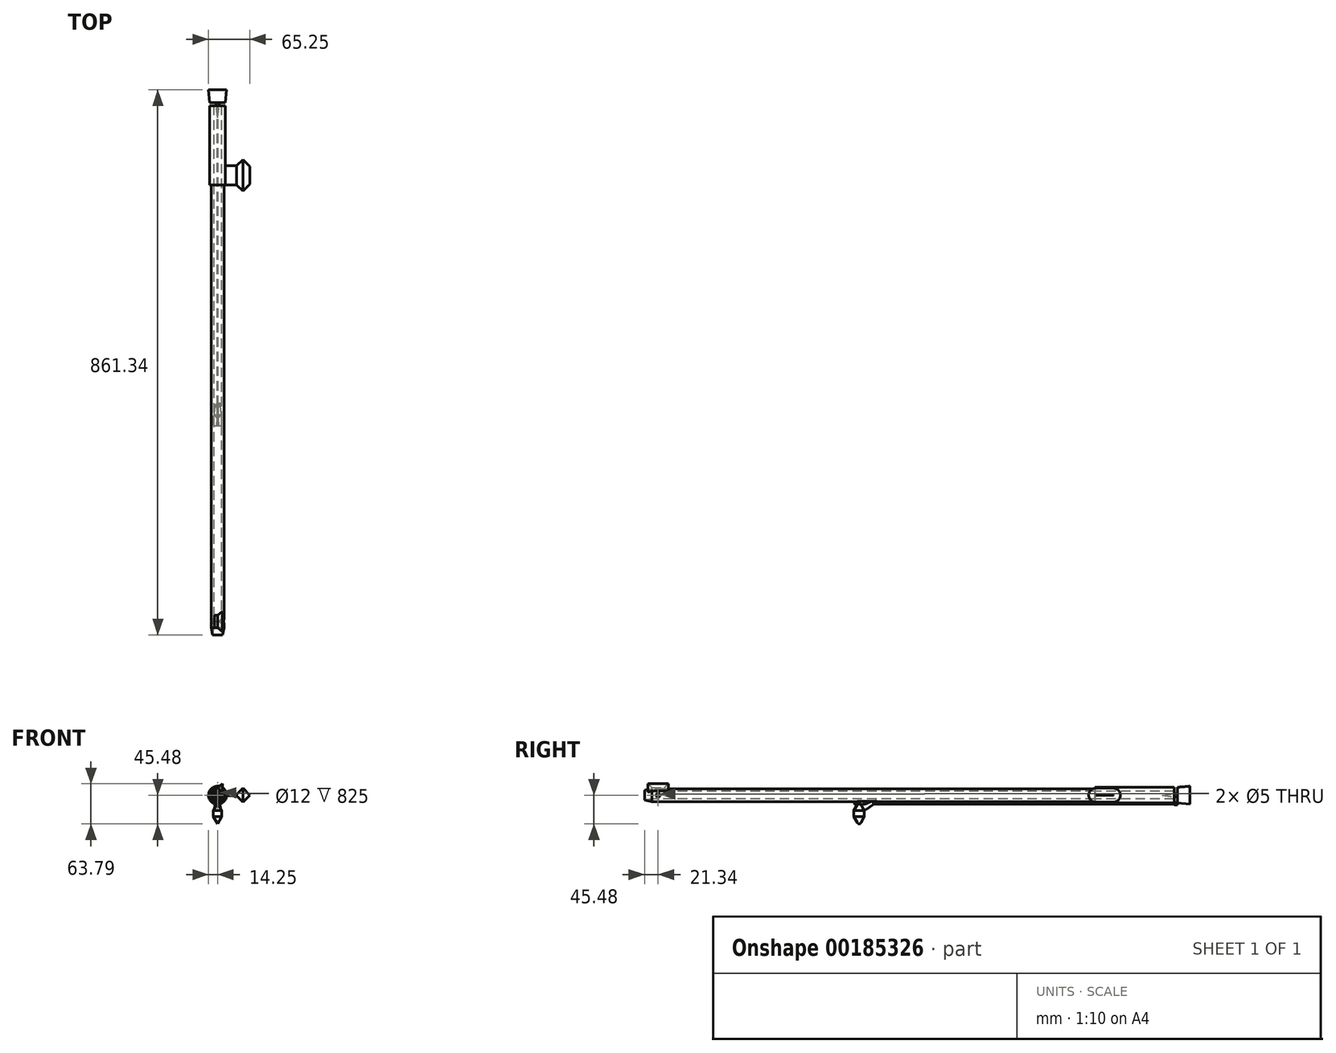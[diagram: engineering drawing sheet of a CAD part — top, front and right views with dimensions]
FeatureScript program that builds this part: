
annotation { "Feature Type Name" : "Feature", "Feature Type Description" : "" }
export const myFeature = defineFeature(function(context is Context, id is Id, definition is map)
    precondition{}
    {
        {
            var Q0;
            Q0=qCreatedBy(makeId("Front.planeOp"),FACE);
            var sketch = newSketch(context, id + "F0", { "sketchPlane" : qUnion([Q0])});
            skCircle(sketch, "E0", {"center": v(0, 0) * mm, "radius": 6 * mm});
            skCircle(sketch, "E1", {"center": v(0, 0) * mm, "radius": 10 * mm});
            skSolve(sketch);
        }
        {
            var Q0;
            Q0=makeQuery(id+"F0.imprint","IMPRINT",FACE,{"disambiguationData":[TD([[makeQuery(id+"F0.imprint","IMPRINT",EDGE,{"derivedFrom":sQuery(id+"F0.wireOp",EDGE,"E0")}),-1.0]])]});
            extrude(context, id + "F1", {"entities" : qUnion([Q0]), "oppositeDirection" : true, "depth" : 700 * mm});
        }
        {
            var Q0;
            Q0=makeQuery(id+"F1.opExtrude","CAP_FACE",FACE,{"disambiguationData":[OSD([sQuery(id+"F0.wireOp",EDGE,"E0"),sQuery(id+"F0.wireOp",EDGE,"E1")])],"isStart":false});
            var sketch = newSketch(context, id + "F2", { "sketchPlane" : qUnion([Q0])});
            skArc(sketch, "E2", {"start": v(0, -10) * mm, "mid": v(10.04, 0) * mm, "end": v(0, 10) * mm});
            skArc(sketch, "E3", {"start": v(0, -6) * mm, "mid": v(5.98, 0) * mm, "end": v(0, 6) * mm});
            skLineSegment(sketch, "E4", {"start": v(0, 6) * mm, "end": v(0, 10) * mm});
            skLineSegment(sketch, "E5", {"start": v(0, -6) * mm, "end": v(0, -10) * mm});
            skSolve(sketch);
        }
        {
            var Q0;
            Q0 = qSketchRegion(id + "F2", true);
            extrude(context, id + "F3", {"entities" : qUnion([Q0]), "operationType" : NewBodyOperationType.ADD, "depth" : 100 * mm});
        }
        {
            var Q0;
            Q0=makeQuery(id+"F1.opExtrude","CAP_FACE",FACE,{"disambiguationData":[OSD([sQuery(id+"F0.wireOp",EDGE,"E0"),sQuery(id+"F0.wireOp",EDGE,"E1")])],"isStart":false});
            var sketch = newSketch(context, id + "F4", { "sketchPlane" : qUnion([Q0])});
            skArc(sketch, "E6", {"start": v(0, 10) * mm, "mid": v(-10, 0) * mm, "end": v(0, -10) * mm});
            skLineSegment(sketch, "E7", {"start": v(0, 10) * mm, "end": v(0, 6) * mm});
            skLineSegment(sketch, "E8", {"start": v(0, -10) * mm, "end": v(0, -6) * mm});
            skArc(sketch, "E9", {"start": v(0, 6) * mm, "mid": v(-6, 0) * mm, "end": v(0, -6) * mm});
            skCircle(sketch, "E10", {"center": v(0, 0) * mm, "radius": 12.5 * mm});
            skCircle(sketch, "E11", {"center": v(0, 0) * mm, "radius": 10 * mm});
            skSolve(sketch);
        }
        {
            var Q0;
            Q0 = qSketchRegion(id + "F4", true);
            extrude(context, id + "F5", {"entities" : qUnion([Q0]), "depth" : 100 * mm});
        }
        {
            var Q0;
            Q0=makeQuery(id+"F1.opExtrude","CAP_FACE",FACE,{"disambiguationData":[OSD([sQuery(id+"F0.wireOp",EDGE,"E0"),sQuery(id+"F0.wireOp",EDGE,"E1")])],"isStart":false});
            extrude(context, id + "F6", {"entities" : qUnion([Q0]), "operationType" : NewBodyOperationType.ADD, "depth" : 100 * mm});
        }
        {
            var Q0;
            Q0=makeQuery(id+"F3.opExtrude","CAP_FACE",FACE,{"disambiguationData":[OSD([sQuery(id+"F2.wireOp",EDGE,"E2"),sQuery(id+"F2.wireOp",EDGE,"E3"),sQuery(id+"F2.wireOp",EDGE,"E4"),sQuery(id+"F2.wireOp",EDGE,"E5")])],"isStart":false});
            var sketch = newSketch(context, id + "F7", { "sketchPlane" : qUnion([Q0])});
            skCircle(sketch, "E12", {"center": v(0, 0) * mm, "radius": 12.5 * mm});
            skSolve(sketch);
        }
        {
            var Q0;
            Q0=makeQuery(id+"F7.imprint","IMPRINT",FACE,{"disambiguationData":[TD([[makeQuery(id+"F7.imprint","IMPRINT",EDGE,{"derivedFrom":sQuery(id+"F7.wireOp",EDGE,"E12")}),1.0]])]});
            var Q1;
            Q1=makeQuery(id+"F7.imprint","IMPRINT",FACE,{"disambiguationData":[TD([[makeQuery(id+"F7.imprint","IMPRINT",EDGE,{"derivedFrom":makeQuery(id+"F3.opExtrude","CAP_EDGE",EDGE,{"disambiguationData":[OSD([sQuery(id+"F2.wireOp",EDGE,"E2")])],"isStart":false})}),1.0]])]});
            extrude(context, id + "F8", {"entities" : qUnion([Q0, Q1]), "operationType" : NewBodyOperationType.ADD, "depth" : 25 * mm});
        }
        {
            var Q0;
            Q0=makeQuery(id+"F6.boolean.opBoolean","MERGE",FACE,{"derivedFrom":[makeQuery(id+"F5.opExtrude","CAP_FACE",FACE,{"disambiguationData":[OSD([sQuery(id+"F4.wireOp",EDGE,"E10"),sQuery(id+"F4.wireOp",EDGE,"E11")])],"isStart":true}),makeQuery(id+"F6.opExtrude","CAP_FACE",FACE,{"disambiguationData":[OSD([sQuery(id+"F0.wireOp",EDGE,"E0"),sQuery(id+"F0.wireOp",EDGE,"E1")])],"isStart":true})]});
            var sketch = newSketch(context, id + "F9", { "sketchPlane" : qUnion([Q0])});
            skLineSegment(sketch, "E13", {"start": v(10, 0) * mm, "end": v(10, 1) * mm});
            skLineSegment(sketch, "E14", {"start": v(10, 1) * mm, "end": v(30, 1) * mm});
            skLineSegment(sketch, "E15", {"start": v(30, 1) * mm, "end": v(30, -1) * mm});
            skLineSegment(sketch, "E16", {"start": v(30, -1) * mm, "end": v(10, -1) * mm});
            skLineSegment(sketch, "E17", {"start": v(10, -1) * mm, "end": v(10, 0) * mm});
            skSolve(sketch);
        }
        {
            var Q0;
            {var subQ0=sQuery(id+"F9.wireOp",EDGE,"E15");Q0=makeQuery(id+"F9.imprint","IMPRINT",FACE,{"disambiguationData":[TD([[makeQuery(id+"F9.imprint","IMPRINT",EDGE,{"derivedFrom":subQ0}),-1.0]])]});}
            extrude(context, id + "F10", {"entities" : qUnion([Q0]), "operationType" : NewBodyOperationType.ADD, "oppositeDirection" : true, "depth" : 30 * mm});
        }
        {
            var Q0;
            Q0=makeQuery(id+"F10.opExtrude","CAP_EDGE",EDGE,{"disambiguationData":[OSD([sQuery(id+"F9.wireOp",EDGE,"E16")])],"isStart":true});
            var Q1;
            Q1=makeQuery(id+"F10.opExtrude","CAP_EDGE",EDGE,{"disambiguationData":[OSD([sQuery(id+"F9.wireOp",EDGE,"E14")])],"isStart":true});
            var Q2;
            Q2=makeQuery(id+"F10.opExtrude","CAP_EDGE",EDGE,{"disambiguationData":[OSD([sQuery(id+"F9.wireOp",EDGE,"E14")])],"isStart":false});
            var Q3;
            Q3=makeQuery(id+"F10.opExtrude","CAP_EDGE",EDGE,{"disambiguationData":[OSD([sQuery(id+"F9.wireOp",EDGE,"E16")])],"isStart":false});
            fillet(context, id + "F11", {"entities" : qUnion([Q0, Q1, Q2, Q3]), "radius" : 1 * mm, "tangentPropagation" : true, "allowEdgeOverflow" : false});
        }
        {
            var Q0;
            Q0=makeQuery(id+"F10.opExtrude","SWEPT_FACE",FACE,{"disambiguationData":[OSD([sQuery(id+"F9.wireOp",EDGE,"E15")])]});
            extrude(context, id + "F12", {"entities" : qUnion([Q0]), "operationType" : NewBodyOperationType.ADD, "depth" : 10 * mm, "hasDraft" : true, "draftAngle" : 45 * degree});
        }
        {
            var Q0;
            Q0=makeQuery(id+"F12.opExtrude","CAP_FACE",FACE,{"disambiguationData":[OSD([sQuery(id+"F9.wireOp",EDGE,"E15")])],"isStart":false});
            extrude(context, id + "F13", {"entities" : qUnion([Q0]), "operationType" : NewBodyOperationType.ADD, "depth" : 25 * mm, "hasDraft" : true, "draftAngle" : 45 * degree, "draftPullDirection" : true});
        }
        {
            var Q0;
            Q0=makeQuery(id+"F8.opExtrude","CAP_FACE",FACE,{"disambiguationData":[OSD([sQuery(id+"F7.wireOp",EDGE,"E12")])],"isStart":false});
            var sketch = newSketch(context, id + "F14", { "sketchPlane" : qUnion([Q0])});
            skPoint(sketch, "E18", {"position": v(0, 0) * mm});
            skSolve(sketch);
        }
        {
            var Q0;
            Q0=sQuery(id+"F14.wireOp",VERTEX,"E18");
            var Q1;
            Q1=makeQuery(id+"F1.opExtrude","SWEPT_BODY",BODY,{"disambiguationData":[OSD([sQuery(id+"F0.wireOp",EDGE,"E0"),sQuery(id+"F0.wireOp",EDGE,"E1")])]});
            hole(context, id + "F15", {"style" : HoleStyle.SIMPLE, "endStyle" : HoleEndStyle.THROUGH, "holeDiameter" : 5 * mm, "locations" : qUnion([Q0]), "scope" : qUnion([Q1]), "isTappedThrough" : true});
        }
        {
            var Q0;
            Q0=makeQuery(id+"F8.opExtrude","CAP_FACE",FACE,{"disambiguationData":[OSD([sQuery(id+"F7.wireOp",EDGE,"E12")])],"isStart":false});
            var sketch = newSketch(context, id + "F16", { "sketchPlane" : qUnion([Q0])});
            skCircle(sketch, "E19", {"center": v(0, 0) * mm, "radius": 2.5 * mm});
            skSolve(sketch);
        }
        {
            var Q0;
            Q0 = qSketchRegion(id + "F16", true);
            extrude(context, id + "F17", {"entities" : qUnion([Q0]), "oppositeDirection" : true, "depth" : 20 * mm, "hasDraft" : true, "draftAngle" : 7.5 * degree, "draftPullDirection" : true});
        }
        {
            var Q0;
            Q0=makeQuery(id+"F17.opExtrude","CAP_FACE",FACE,{"disambiguationData":[OSD([sQuery(id+"F16.wireOp",EDGE,"E19")])],"isStart":true});
            extrude(context, id + "F18", {"entities" : qUnion([Q0]), "operationType" : NewBodyOperationType.ADD, "depth" : 5 * mm});
        }
        {
            var Q0;
            Q0=makeQuery(id+"F18.opExtrude","CAP_FACE",FACE,{"disambiguationData":[OSD([sQuery(id+"F16.wireOp",EDGE,"E19")])],"isStart":false});
            var sketch = newSketch(context, id + "F19", { "sketchPlane" : qUnion([Q0])});
            skCircle(sketch, "E20", {"center": v(0, 0) * mm, "radius": 12.5 * mm});
            skSolve(sketch);
        }
        {
            var Q0;
            Q0 = qSketchRegion(id + "F19", true);
            extrude(context, id + "F20", {"entities" : qUnion([Q0]), "operationType" : NewBodyOperationType.ADD, "depth" : 20 * mm, "hasDraft" : true, "draftAngle" : 5 * degree});
        }
        {
            var Q0;
            Q0=makeQuery(id+"F8.opExtrude","CAP_FACE",FACE,{"disambiguationData":[OSD([sQuery(id+"F7.wireOp",EDGE,"E12")])],"isStart":false});
            var sketch = newSketch(context, id + "F21", { "sketchPlane" : qUnion([Q0])});
            skLineSegment(sketch, "E21", {"start": v(0, -12.5) * mm, "end": v(0, -13.5) * mm});
            skLineSegment(sketch, "E22.bottom", {"start": v(0.5, -15.25) * mm, "end": v(-0.5, -15.25) * mm});
            skLineSegment(sketch, "E22.top", {"start": v(0.5, -11.75) * mm, "end": v(-0.5, -11.75) * mm});
            skLineSegment(sketch, "E22.left", {"start": v(0.5, -15.25) * mm, "end": v(0.5, -11.75) * mm});
            skLineSegment(sketch, "E22.right", {"start": v(-0.5, -15.25) * mm, "end": v(-0.5, -11.75) * mm});
            skPoint(sketch, "E22.middle", {"position": v(0, -13.5) * mm});
            skSolve(sketch);
        }
        {
            var Q0;
            Q0 = qSketchRegion(id + "F21", true);
            extrude(context, id + "F22", {"entities" : qUnion([Q0]), "depth" : 5 * mm});
        }
        {
            var Q0;
            Q0=makeQuery(id+"F22.opExtrude","CAP_FACE",FACE,{"disambiguationData":[OSD([sQuery(id+"F21.wireOp",EDGE,"E22.bottom"),sQuery(id+"F21.wireOp",EDGE,"E22.top"),sQuery(id+"F21.wireOp",EDGE,"E22.left"),sQuery(id+"F21.wireOp",EDGE,"E22.right")])],"isStart":true});
            var sketch = newSketch(context, id + "F23", { "sketchPlane" : qUnion([Q0])});
            skLineSegment(sketch, "E23", {"start": v(0, -11.75) * mm, "end": v(0, -13.5) * mm});
            skPoint(sketch, "E23.endSnap0", {"position": v(0, -15.25) * mm});
            skCircle(sketch, "E24", {"center": v(0, -13.5) * mm, "radius": 0.5 * mm});
            skSolve(sketch);
        }
        {
            var Q0;
            Q0=makeQuery(id+"F23.imprint","IMPRINT",FACE,{"disambiguationData":[TD([[makeQuery(id+"F23.imprint","IMPRINT",EDGE,{"derivedFrom":sQuery(id+"F23.wireOp",EDGE,"E24")}),1.0]])]});
            extrude(context, id + "F24", {"entities" : qUnion([Q0]), "operationType" : NewBodyOperationType.ADD, "depth" : 500 * mm});
        }
        {
            var Q0;
            Q0=makeQuery(id+"F24.opExtrude","CAP_FACE",FACE,{"disambiguationData":[OSD([sQuery(id+"F23.wireOp",EDGE,"E24")])],"isStart":false});
            var sketch = newSketch(context, id + "F25", { "sketchPlane" : qUnion([Q0])});
            skArc(sketch, "E25", {"start": v(-1, -13.5) * mm, "mid": v(0, -14.5) * mm, "end": v(1, -13.5) * mm});
            skLineSegment(sketch, "E26", {"start": v(-1, -13.5) * mm, "end": v(-1, -9.96) * mm});
            skLineSegment(sketch, "E27", {"start": v(1, -13.5) * mm, "end": v(1, -9.96) * mm});
            skLineSegment(sketch, "E28", {"start": v(-1, -9.96) * mm, "end": v(1, -9.96) * mm});
            skSolve(sketch);
        }
        {
            var Q0;
            Q0=makeQuery(id+"F25.imprint","IMPRINT",FACE,{"disambiguationData":[TD([[makeQuery(id+"F25.imprint","IMPRINT",EDGE,{"derivedFrom":sQuery(id+"F25.wireOp",EDGE,"E25")}),1.0]])]});
            extrude(context, id + "F26", {"entities" : qUnion([Q0]), "operationType" : NewBodyOperationType.ADD, "oppositeDirection" : true, "depth" : 25 * mm});
        }
        {
            var Q0;
            Q0=makeQuery(id+"F24.opExtrude","CAP_FACE",FACE,{"disambiguationData":[OSD([sQuery(id+"F23.wireOp",EDGE,"E24")])],"isStart":false});
            var sketch = newSketch(context, id + "F27", { "sketchPlane" : qUnion([Q0])});
            skCircle(sketch, "E29", {"center": v(0, -13.5) * mm, "radius": 0.5 * mm});
            skLineSegment(sketch, "E30", {"start": v(0, -13) * mm, "end": v(2, -13) * mm});
            skLineSegment(sketch, "E31", {"start": v(0, -14) * mm, "end": v(2, -14) * mm});
            skLineSegment(sketch, "E32", {"start": v(2, -14) * mm, "end": v(2, -13) * mm});
            skSolve(sketch);
        }
        {
            var Q0;
            {var subQ0=sQuery(id+"F27.wireOp",EDGE,"E30");Q0=makeQuery(id+"F27.imprint","IMPRINT",FACE,{"disambiguationData":[TD([[makeQuery(id+"F27.imprint","IMPRINT",EDGE,{"derivedFrom":subQ0}),-1.0]])]});}
            var Q1;
            Q1=makeQuery(id+"F27.imprint","IMPRINT",FACE,{"disambiguationData":[TD([[makeQuery(id+"F27.imprint","IMPRINT",EDGE,{"derivedFrom":sQuery(id+"F27.wireOp",EDGE,"E29")}),1.0]])]});
            extrude(context, id + "F28", {"entities" : qUnion([Q0, Q1]), "operationType" : NewBodyOperationType.ADD, "depth" : 5 * mm});
        }
        {
            var Q0;
            Q0=makeQuery(id+"F26.opExtrude","CAP_FACE",FACE,{"disambiguationData":[OSD([sQuery(id+"F23.wireOp",EDGE,"E24"),sQuery(id+"F25.wireOp",EDGE,"E25"),sQuery(id+"F25.wireOp",EDGE,"E26"),sQuery(id+"F25.wireOp",EDGE,"E27"),sQuery(id+"F25.wireOp",EDGE,"E28")])],"isStart":true});
            var sketch = newSketch(context, id + "F29", { "sketchPlane" : qUnion([Q0])});
            skLineSegment(sketch, "E33", {"start": v(0, -14) * mm, "end": v(0.87, -14) * mm});
            skLineSegment(sketch, "E34", {"start": v(0.87, -14) * mm, "end": v(-0.87, -14) * mm});
            skSolve(sketch);
        }
        {
            var Q0;
            {var subQ0=sQuery(id+"F29.wireOp",EDGE,"E34");var subQ1=makeQuery(id+"F26.opExtrude","CAP_EDGE",EDGE,{"disambiguationData":[OSD([sQuery(id+"F25.wireOp",EDGE,"E25")])],"isStart":true});var subQ2=makeQuery(id+"F29.imprint","INTERSECT",VERTEX,{"disambiguationData":[OD(0.0)],"derivedFrom":[subQ1,subQ0]});Q0=makeQuery(id+"F29.imprint","IMPRINT",FACE,{"disambiguationData":[TD([[makeQuery(id+"F29.imprint","IMPRINT",EDGE,{"disambiguationData":[TD([[subQ2,-1.0]])],"derivedFrom":subQ0}),1.0]])]});}
            extrude(context, id + "F30", {"entities" : qUnion([Q0]), "operationType" : NewBodyOperationType.ADD, "depth" : 5 * mm});
        }
        {
            var Q0;
            Q0=makeQuery(id+"F28.opExtrude","SWEPT_FACE",FACE,{"disambiguationData":[OSD([sQuery(id+"F27.wireOp",EDGE,"E31")])]});
            var sketch = newSketch(context, id + "F31", { "sketchPlane" : qUnion([Q0])});
            skLineSegment(sketch, "E35", {"start": v(0, -320) * mm, "end": v(0, -325) * mm});
            skLineSegment(sketch, "E36", {"start": v(0, -325) * mm, "end": v(-0.85, -325) * mm});
            skLineSegment(sketch, "E37", {"start": v(0, -325) * mm, "end": v(0.85, -325) * mm});
            skLineSegment(sketch, "E38.bottom", {"start": v(-0.85, -325) * mm, "end": v(0.86, -325) * mm});
            skLineSegment(sketch, "E38.top", {"start": v(-0.85, -330.01) * mm, "end": v(0.86, -330.01) * mm});
            skLineSegment(sketch, "E38.left", {"start": v(-0.85, -325) * mm, "end": v(-0.85, -330.01) * mm});
            skLineSegment(sketch, "E38.right", {"start": v(0.86, -325) * mm, "end": v(0.86, -330.01) * mm});
            skSolve(sketch);
        }
        {
            var Q0;
            Q0 = qSketchRegion(id + "F31", true);
            extrude(context, id + "F32", {"entities" : qUnion([Q0]), "operationType" : NewBodyOperationType.ADD, "depth" : 10 * mm, "hasDraft" : true, "draftAngle" : 30 * degree});
        }
        {
            var Q0;
            Q0=makeQuery(id+"F32.opExtrude","CAP_FACE",FACE,{"disambiguationData":[OSD([sQuery(id+"F31.wireOp",EDGE,"E38.bottom"),sQuery(id+"F31.wireOp",EDGE,"E38.top"),sQuery(id+"F31.wireOp",EDGE,"E38.left"),sQuery(id+"F31.wireOp",EDGE,"E38.right")])],"isStart":false});
            extrude(context, id + "F33", {"entities" : qUnion([Q0]), "operationType" : NewBodyOperationType.ADD, "depth" : 10 * mm});
        }
        {
            var Q0;
            Q0=makeQuery(id+"F33.opExtrude","CAP_FACE",FACE,{"disambiguationData":[OSD([sQuery(id+"F31.wireOp",EDGE,"E38.bottom"),sQuery(id+"F31.wireOp",EDGE,"E38.top"),sQuery(id+"F31.wireOp",EDGE,"E38.left"),sQuery(id+"F31.wireOp",EDGE,"E38.right")])],"isStart":false});
            extrude(context, id + "F34", {"entities" : qUnion([Q0]), "operationType" : NewBodyOperationType.ADD, "depth" : 25 * mm, "hasDraft" : true, "draftAngle" : 30 * degree, "draftPullDirection" : true});
        }
        {
            var Q0;
            Q0=makeQuery(id+"F32.opExtrude","SWEPT_EDGE",EDGE,{"disambiguationData":[OSD([sQuery(id+"F31.wireOp",EDGE,"E38.top"),sQuery(id+"F31.wireOp",EDGE,"E38.right")])]});
            var Q1;
            Q1=makeQuery(id+"F32.opExtrude","SWEPT_EDGE",EDGE,{"disambiguationData":[OSD([sQuery(id+"F31.wireOp",EDGE,"E38.top"),sQuery(id+"F31.wireOp",EDGE,"E38.left")])]});
            var Q2;
            Q2=makeQuery(id+"F32.opExtrude","SWEPT_EDGE",EDGE,{"disambiguationData":[OSD([sQuery(id+"F31.wireOp",EDGE,"E38.bottom"),sQuery(id+"F31.wireOp",EDGE,"E38.right")])]});
            var Q3;
            Q3=makeQuery(id+"F32.opExtrude","SWEPT_EDGE",EDGE,{"disambiguationData":[OSD([sQuery(id+"F31.wireOp",EDGE,"E36"),sQuery(id+"F31.wireOp",EDGE,"E38.bottom"),sQuery(id+"F31.wireOp",EDGE,"E38.left")])]});
            var Q4;
            Q4=makeQuery(id+"F33.opExtrude","SWEPT_EDGE",EDGE,{"disambiguationData":[OSD([sQuery(id+"F31.wireOp",EDGE,"E38.bottom"),sQuery(id+"F31.wireOp",EDGE,"E38.right")])]});
            var Q5;
            Q5=makeQuery(id+"F33.opExtrude","SWEPT_EDGE",EDGE,{"disambiguationData":[OSD([sQuery(id+"F31.wireOp",EDGE,"E38.top"),sQuery(id+"F31.wireOp",EDGE,"E38.right")])]});
            var Q6;
            Q6=makeQuery(id+"F33.opExtrude","SWEPT_EDGE",EDGE,{"disambiguationData":[OSD([sQuery(id+"F31.wireOp",EDGE,"E38.top"),sQuery(id+"F31.wireOp",EDGE,"E38.left")])]});
            var Q7;
            Q7=makeQuery(id+"F33.opExtrude","SWEPT_EDGE",EDGE,{"disambiguationData":[OSD([sQuery(id+"F31.wireOp",EDGE,"E36"),sQuery(id+"F31.wireOp",EDGE,"E38.bottom"),sQuery(id+"F31.wireOp",EDGE,"E38.left")])]});
            var Q8;
            Q8=makeQuery(id+"F34.opExtrude","SWEPT_EDGE",EDGE,{"disambiguationData":[OSD([sQuery(id+"F31.wireOp",EDGE,"E36"),sQuery(id+"F31.wireOp",EDGE,"E38.bottom"),sQuery(id+"F31.wireOp",EDGE,"E38.left")])]});
            var Q9;
            Q9=makeQuery(id+"F34.opExtrude","SWEPT_EDGE",EDGE,{"disambiguationData":[OSD([sQuery(id+"F31.wireOp",EDGE,"E38.top"),sQuery(id+"F31.wireOp",EDGE,"E38.left")])]});
            var Q10;
            Q10=makeQuery(id+"F34.opExtrude","SWEPT_EDGE",EDGE,{"disambiguationData":[OSD([sQuery(id+"F31.wireOp",EDGE,"E38.top"),sQuery(id+"F31.wireOp",EDGE,"E38.right")])]});
            var Q11;
            Q11=makeQuery(id+"F34.opExtrude","SWEPT_EDGE",EDGE,{"disambiguationData":[OSD([sQuery(id+"F31.wireOp",EDGE,"E38.bottom"),sQuery(id+"F31.wireOp",EDGE,"E38.right")])]});
            fillet(context, id + "F35", {"entities" : qUnion([Q0, Q1, Q2, Q3, Q4, Q5, Q6, Q7, Q8, Q9, Q10, Q11]), "radius" : 1.5 * mm, "tangentPropagation" : true, "allowEdgeOverflow" : false});
        }
        {
            var Q0;
            Q0=makeQuery(id+"F32.opExtrude","SWEPT_FACE",FACE,{"disambiguationData":[OSD([sQuery(id+"F31.wireOp",EDGE,"E38.top")])]});
            extrude(context, id + "F36", {"entities" : qUnion([Q0]), "operationType" : NewBodyOperationType.ADD, "depth" : 20 * mm, "hasDraft" : true, "draftAngle" : 3 * degree, "draftPullDirection" : true});
        }
        {
            var Q0;
            {var subQ0=sQuery(id+"F31.wireOp",EDGE,"E38.top");var subQ1=sQuery(id+"F31.wireOp",EDGE,"E38.left");Q0=makeQuery(id+"F36.opExtrude","CAP_EDGE",EDGE,{"disambiguationData":[OSD([subQ0,subQ1]),TDD([makeQuery(id+"F35.opFillet","BLEND_EDGE",EDGE,{"blendedFrom":[makeQuery(id+"F32.opExtrude","SWEPT_EDGE",EDGE,{"disambiguationData":[OSD([subQ0,subQ1])]}),makeQuery(id+"F32.opExtrude","SWEPT_FACE",FACE,{"disambiguationData":[OSD([subQ0])]})],"blendedInto":[makeQuery(id+"F32.opExtrude","SWEPT_FACE",FACE,{"disambiguationData":[OSD([subQ0])]})]})])],"isStart":false});}
            var Q1;
            {var subQ0=sQuery(id+"F31.wireOp",EDGE,"E38.top");var subQ1=sQuery(id+"F31.wireOp",EDGE,"E38.right");Q1=makeQuery(id+"F36.opExtrude","CAP_EDGE",EDGE,{"disambiguationData":[OSD([subQ0,subQ1]),TDD([makeQuery(id+"F35.opFillet","BLEND_EDGE",EDGE,{"blendedFrom":[makeQuery(id+"F32.opExtrude","SWEPT_EDGE",EDGE,{"disambiguationData":[OSD([subQ0,subQ1])]}),makeQuery(id+"F32.opExtrude","SWEPT_FACE",FACE,{"disambiguationData":[OSD([subQ0])]})],"blendedInto":[makeQuery(id+"F32.opExtrude","SWEPT_FACE",FACE,{"disambiguationData":[OSD([subQ0])]})]})])],"isStart":false});}
            chamfer(context, id + "F37", {"entities" : qUnion([Q0, Q1]), "chamferType" : ChamferType.OFFSET_ANGLE, "width" : 4 * mm, "oppositeDirection" : false, "angle" : 25 * degree, "tangentPropagation" : true});
        }
        {
            var Q0;
            Q0=makeQuery(id+"F37.opChamfer","BLEND_FACE",FACE,{"disambiguationData":[OSD([sQuery(id+"F31.wireOp",EDGE,"E38.top"),sQuery(id+"F31.wireOp",EDGE,"E38.right")])]});
            var Q1;
            Q1=makeQuery(id+"F37.opChamfer","BLEND_FACE",FACE,{"disambiguationData":[OSD([sQuery(id+"F31.wireOp",EDGE,"E38.top"),sQuery(id+"F31.wireOp",EDGE,"E38.left")])]});
            extrude(context, id + "F38", {"entities" : qUnion([Q0, Q1]), "operationType" : NewBodyOperationType.ADD, "depth" : 5 * mm, "hasDraft" : true, "draftAngle" : 10 * degree, "draftPullDirection" : true});
        }
        {
            var Q0;
            Q0=qCreatedBy(makeId("Right.planeOp"),FACE);
            var sketch = newSketch(context, id + "F39", { "sketchPlane" : qUnion([Q0])});
            skLineSegment(sketch, "E39", {"start": v(0, 10.01) * mm, "end": v(10, 10.01) * mm});
            skLineSegment(sketch, "E40", {"start": v(10, 10.01) * mm, "end": v(10, 0) * mm});
            skPoint(sketch, "E41", {"position": v(10, 0) * mm});
            skSolve(sketch);
        }
        {
            var Q0;
            Q0=sQuery(id+"F39.wireOp",VERTEX,"E41");
            var Q1;
            Q1=makeQuery(id+"F1.opExtrude","SWEPT_BODY",BODY,{"disambiguationData":[OSD([sQuery(id+"F0.wireOp",EDGE,"E0"),sQuery(id+"F0.wireOp",EDGE,"E1")])]});
            hole(context, id + "F40", {"style" : HoleStyle.C_SINK, "endStyle" : HoleEndStyle.BLIND, "holeDiameter" : 5 * mm, "cSinkDiameter" : 12.5 * mm, "cSinkAngle" : 45 * degree, "holeDepth" : 100 * mm, "startFromSketch" : true, "locations" : qUnion([Q0]), "scope" : qUnion([Q1])});
        }
        {
            var Q0;
            Q0=sQuery(id+"F39.wireOp",VERTEX,"E41");
            var Q1;
            Q1=makeQuery(id+"F1.opExtrude","SWEPT_BODY",BODY,{"disambiguationData":[OSD([sQuery(id+"F0.wireOp",EDGE,"E0"),sQuery(id+"F0.wireOp",EDGE,"E1")])]});
            hole(context, id + "F41", {"style" : HoleStyle.C_SINK, "endStyle" : HoleEndStyle.BLIND, "oppositeDirection" : true, "holeDiameter" : 5 * mm, "cSinkDiameter" : 12.5 * mm, "cSinkAngle" : 45 * degree, "holeDepth" : 100 * mm, "startFromSketch" : true, "locations" : qUnion([Q0]), "scope" : qUnion([Q1])});
        }
        {
            var Q0;
            Q0=makeQuery(id+"F0.imprint","IMPRINT",FACE,{"disambiguationData":[TD([[makeQuery(id+"F0.imprint","IMPRINT",EDGE,{"derivedFrom":sQuery(id+"F0.wireOp",EDGE,"E0")}),-1.0]])]});
            extrude(context, id + "F42", {"entities" : qUnion([Q0]), "operationType" : NewBodyOperationType.ADD, "depth" : 20 * mm, "hasDraft" : true, "draftAngle" : 10 * degree, "draftPullDirection" : true});
        }
        {
            var Q0;
            Q0=qCreatedBy(makeId("Right.planeOp"),FACE);
            var sketch = newSketch(context, id + "F43", { "sketchPlane" : qUnion([Q0])});
            skLineSegment(sketch, "E42.bottom", {"start": v(0, 10) * mm, "end": v(19.93, 10) * mm});
            skLineSegment(sketch, "E42.top", {"start": v(0, 12.02) * mm, "end": v(19.93, 12.02) * mm});
            skLineSegment(sketch, "E42.left", {"start": v(0, 10) * mm, "end": v(0, 12.02) * mm});
            skLineSegment(sketch, "E42.right", {"start": v(19.93, 10) * mm, "end": v(19.93, 12.02) * mm});
            skSolve(sketch);
        }
        {
            var Q0;
            Q0 = qSketchRegion(id + "F43", true);
            var Q1;
            Q1=makeQuery(id+"F43.imprint","IMPRINT",FACE,{"disambiguationData":[TD([[makeQuery(id+"F43.imprint","IMPRINT",EDGE,{"derivedFrom":sQuery(id+"F43.wireOp",EDGE,"E42.bottom")}),1.0]])]});
            extrude(context, id + "F44", {"entities" : qUnion([Q0, Q1]), "operationType" : NewBodyOperationType.ADD, "depth" : 7.5 * mm, "hasDraft" : true, "draftAngle" : 40 * degree});
        }
        {
            var Q0;
            Q0=makeQuery(id+"F44.opExtrude","CAP_FACE",FACE,{"disambiguationData":[OSD([sQuery(id+"F43.wireOp",EDGE,"E42.bottom"),sQuery(id+"F43.wireOp",EDGE,"E42.top"),sQuery(id+"F43.wireOp",EDGE,"E42.left"),sQuery(id+"F43.wireOp",EDGE,"E42.right")])],"isStart":true});
            extrude(context, id + "F45", {"entities" : qUnion([Q0]), "operationType" : NewBodyOperationType.ADD, "depth" : 5 * mm, "hasDraft" : true, "draftAngle" : 0 * degree});
        }
    });
